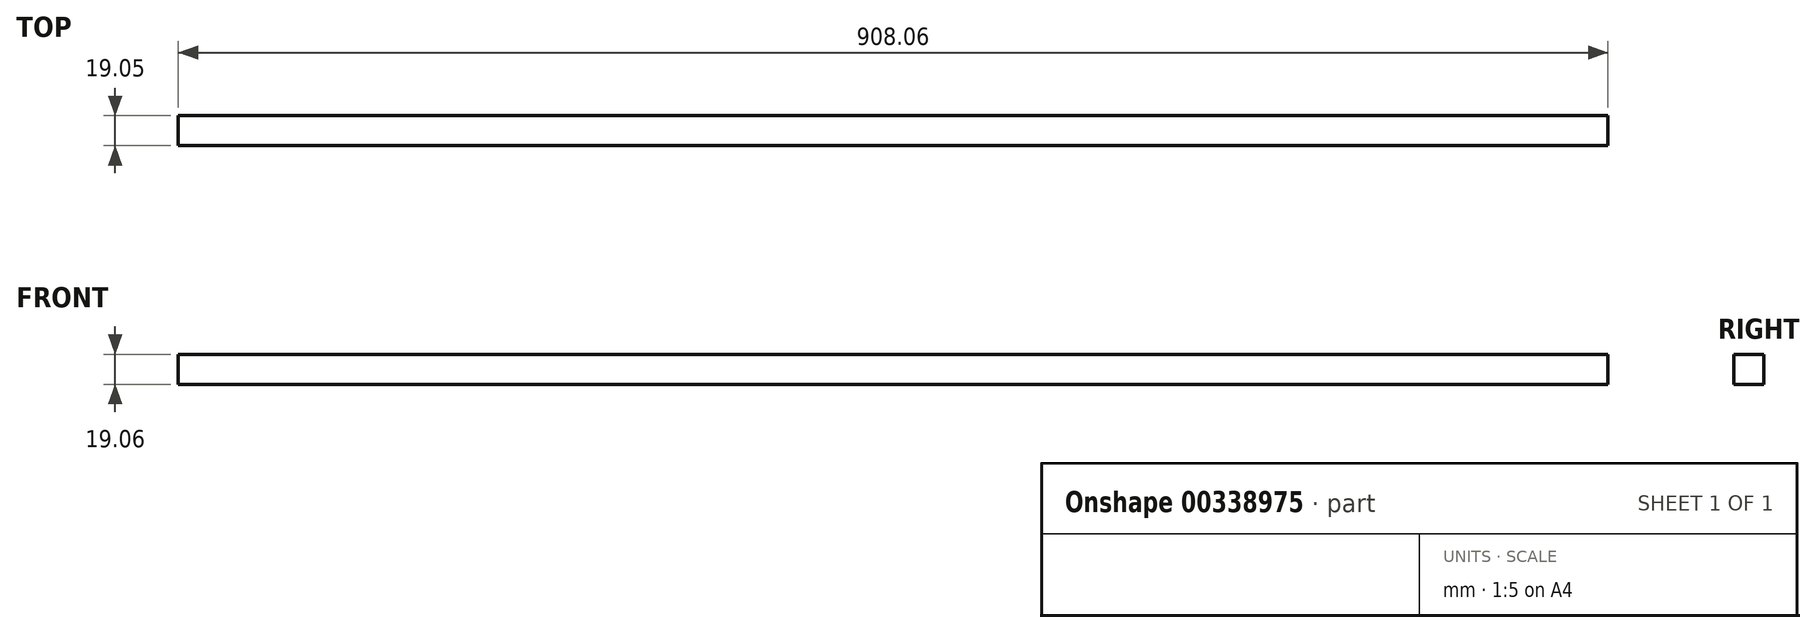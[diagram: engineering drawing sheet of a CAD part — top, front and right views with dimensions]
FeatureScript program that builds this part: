
annotation { "Feature Type Name" : "Feature", "Feature Type Description" : "" }
export const myFeature = defineFeature(function(context is Context, id is Id, definition is map)
    precondition{}
    {
        {
            var Q0;
            Q0=qCreatedBy(makeId("Front.planeOp"),FACE);
            var sketch = newSketch(context, id + "F0", { "sketchPlane" : qUnion([Q0])});
            skLineSegment(sketch, "E0.bottom", {"start": v(454.03, 9.53) * mm, "end": v(-454.03, 9.53) * mm});
            skLineSegment(sketch, "E0.top", {"start": v(454.03, -9.53) * mm, "end": v(-454.03, -9.53) * mm});
            skLineSegment(sketch, "E0.left", {"start": v(454.03, 9.53) * mm, "end": v(454.03, -9.53) * mm});
            skLineSegment(sketch, "E0.right", {"start": v(-454.03, 9.53) * mm, "end": v(-454.03, -9.53) * mm});
            skPoint(sketch, "E0.middle", {"position": v(0, 0) * mm});
            skSolve(sketch);
        }
        {
            var Q0;
            Q0 = qSketchRegion(id + "F0", true);
            extrude(context, id + "F1", {"entities" : qUnion([Q0]), "depth" : 19.05 * mm});
        }
    });
